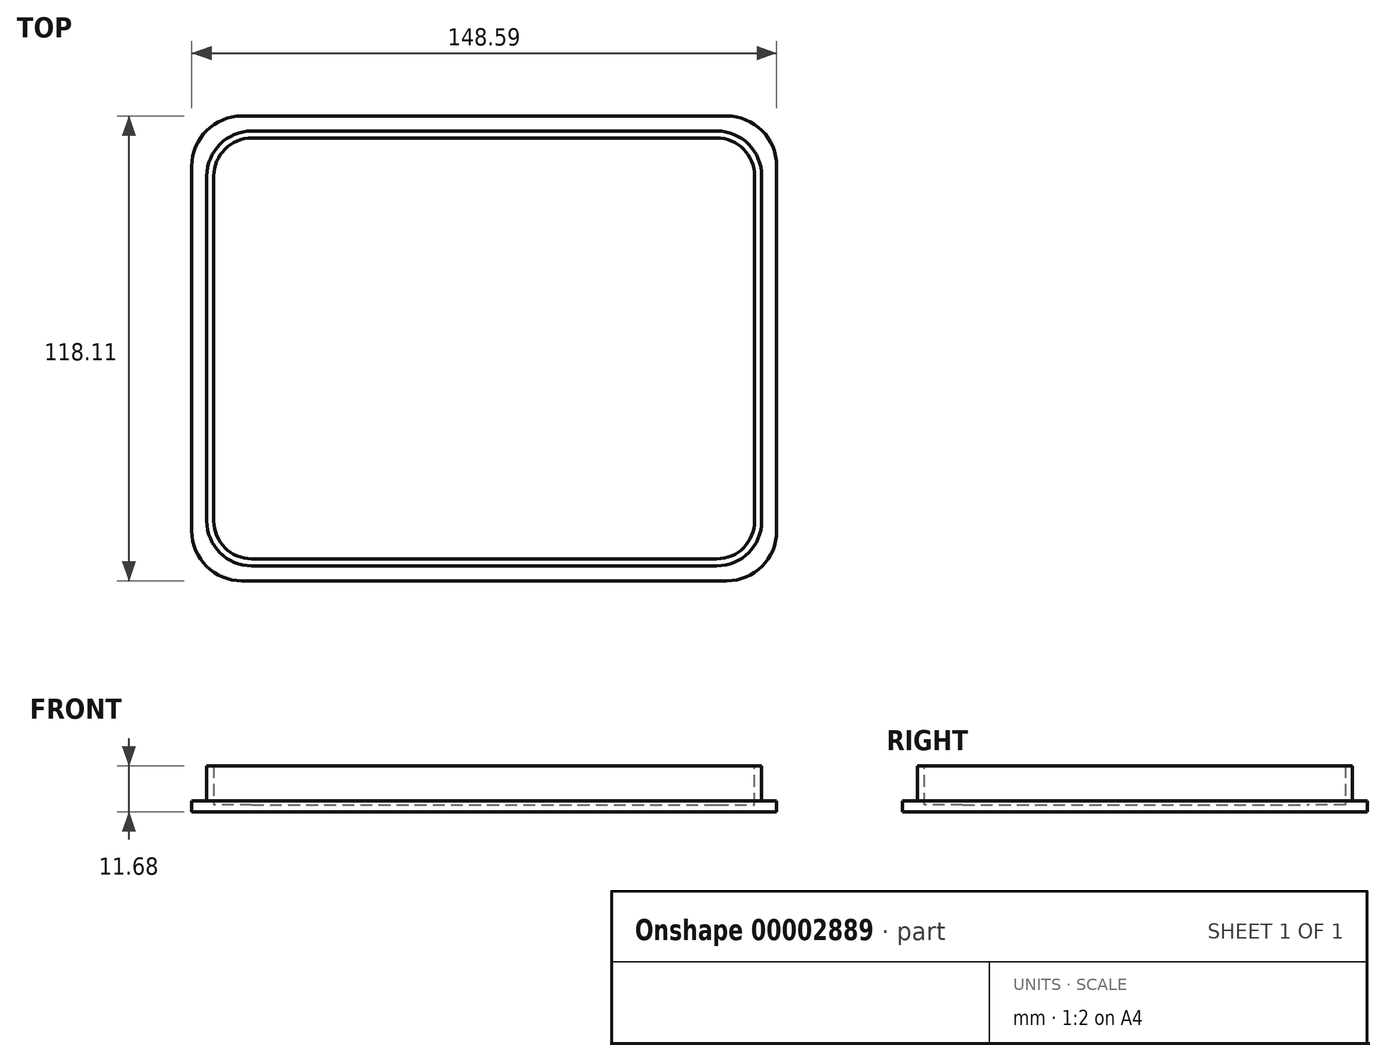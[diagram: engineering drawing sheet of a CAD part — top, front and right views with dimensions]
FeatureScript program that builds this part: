
annotation { "Feature Type Name" : "Feature", "Feature Type Description" : "" }
export const myFeature = defineFeature(function(context is Context, id is Id, definition is map)
    precondition{}
    {
        {
            var Q0;
            Q0=qCreatedBy(makeId("Top.planeOp"),FACE);
            var sketch = newSketch(context, id + "F0", { "sketchPlane" : qUnion([Q0])});
            skLineSegment(sketch, "E0.bottom", {"start": v(12.7, 0) * mm, "end": v(135.9, 0) * mm});
            skLineSegment(sketch, "E0.top", {"start": v(12.7, 118.11) * mm, "end": v(135.89, 118.11) * mm});
            skLineSegment(sketch, "E0.left", {"start": v(0, 12.7) * mm, "end": v(0, 105.41) * mm});
            skLineSegment(sketch, "E0.right", {"start": v(148.6, 12.7) * mm, "end": v(148.59, 105.41) * mm});
            skPoint(sketch, "E1.visualSharp", {"position": v(0, 118.11) * mm});
            skArc(sketch, "E1.filletArc", {"start": v(12.7, 118.11) * mm, "mid": v(3.72, 114.4) * mm, "end": v(0, 105.41) * mm});
            skPoint(sketch, "E2.visualSharp", {"position": v(148.59, 118.11) * mm});
            skArc(sketch, "E2.filletArc", {"start": v(148.59, 105.41) * mm, "mid": v(144.87, 114.4) * mm, "end": v(135.89, 118.11) * mm});
            skPoint(sketch, "E3.visualSharp", {"position": v(148.6, 0) * mm});
            skArc(sketch, "E3.filletArc", {"start": v(135.9, 0) * mm, "mid": v(144.87, 3.72) * mm, "end": v(148.6, 12.7) * mm});
            skPoint(sketch, "E4.visualSharp", {"position": v(0, 0) * mm});
            skArc(sketch, "E4.filletArc", {"start": v(0, 12.7) * mm, "mid": v(3.72, 3.72) * mm, "end": v(12.7, 0) * mm});
            skSolve(sketch);
        }
        {
            var Q0;
            Q0=makeQuery(id+"F0.imprint","IMPRINT",FACE,{"disambiguationData":[TD([[makeQuery(id+"F0.imprint","IMPRINT",EDGE,{"derivedFrom":sQuery(id+"F0.wireOp",EDGE,"E0.bottom")}),1.0]])]});
            extrude(context, id + "F1", {"entities" : qUnion([Q0]), "depth" : 2.8 * mm, "offsetDistance" : 25.4 * mm});
        }
        {
            var Q0;
            Q0=makeQuery(id+"F1.opExtrude","CAP_FACE",FACE,{"disambiguationData":[OSD([sQuery(id+"F0.wireOp",EDGE,"E0.bottom"),sQuery(id+"F0.wireOp",EDGE,"E0.top"),sQuery(id+"F0.wireOp",EDGE,"E0.left"),sQuery(id+"F0.wireOp",EDGE,"E0.right"),sQuery(id+"F0.wireOp",EDGE,"E1.filletArc"),sQuery(id+"F0.wireOp",EDGE,"E2.filletArc"),sQuery(id+"F0.wireOp",EDGE,"E3.filletArc"),sQuery(id+"F0.wireOp",EDGE,"E4.filletArc")])],"isStart":false});
            var sketch = newSketch(context, id + "F2", { "sketchPlane" : qUnion([Q0])});
            skLineSegment(sketch, "E5.0.0", {"start": v(135.89, 118.11) * mm, "end": v(12.7, 118.11) * mm});
            skArc(sketch, "E5.0.1", {"start": v(12.7, 118.11) * mm, "mid": v(3.72, 114.4) * mm, "end": v(0, 105.41) * mm});
            skLineSegment(sketch, "E5.0.2", {"start": v(0, 105.41) * mm, "end": v(0, 12.7) * mm});
            skArc(sketch, "E5.0.3", {"start": v(0, 12.7) * mm, "mid": v(3.72, 3.72) * mm, "end": v(12.7, 0) * mm});
            skLineSegment(sketch, "E5.0.4", {"start": v(12.7, 0) * mm, "end": v(135.9, 0) * mm});
            skArc(sketch, "E5.0.5", {"start": v(135.9, 0) * mm, "mid": v(144.87, 3.72) * mm, "end": v(148.6, 12.7) * mm});
            skLineSegment(sketch, "E5.0.6", {"start": v(148.6, 12.7) * mm, "end": v(148.6, 105.41) * mm});
            skArc(sketch, "E5.0.7", {"start": v(148.6, 105.41) * mm, "mid": v(144.87, 114.4) * mm, "end": v(135.89, 118.11) * mm});
            skLineSegment(sketch, "E6.0", {"start": v(133.35, 114.3) * mm, "end": v(15.24, 114.3) * mm});
            skLineSegment(sketch, "E6.1", {"start": v(144.78, 15.24) * mm, "end": v(144.78, 102.87) * mm});
            skLineSegment(sketch, "E6.2", {"start": v(15.24, 3.8) * mm, "end": v(133.35, 3.8) * mm});
            skLineSegment(sketch, "E6.3", {"start": v(3.8, 102.87) * mm, "end": v(3.8, 15.24) * mm});
            skPoint(sketch, "E7.visualSharp", {"position": v(3.8, 114.3) * mm});
            skArc(sketch, "E7.filletArc", {"start": v(15.24, 114.3) * mm, "mid": v(7.16, 110.95) * mm, "end": v(3.8, 102.87) * mm});
            skPoint(sketch, "E8.visualSharp", {"position": v(144.78, 114.3) * mm});
            skArc(sketch, "E8.filletArc", {"start": v(144.78, 102.87) * mm, "mid": v(141.43, 110.95) * mm, "end": v(133.35, 114.3) * mm});
            skPoint(sketch, "E9.visualSharp", {"position": v(144.78, 3.8) * mm});
            skArc(sketch, "E9.filletArc", {"start": v(133.35, 3.8) * mm, "mid": v(141.43, 7.16) * mm, "end": v(144.78, 15.24) * mm});
            skPoint(sketch, "E10.visualSharp", {"position": v(3.8, 3.8) * mm});
            skArc(sketch, "E10.filletArc", {"start": v(3.8, 15.24) * mm, "mid": v(7.16, 7.16) * mm, "end": v(15.24, 3.8) * mm});
            skSolve(sketch);
        }
        {
            var Q0;
            Q0=makeQuery(id+"F2.imprint","IMPRINT",FACE,{"disambiguationData":[TD([[makeQuery(id+"F2.imprint","IMPRINT",EDGE,{"derivedFrom":sQuery(id+"F2.wireOp",EDGE,"E6.0")}),1.0]])]});
            extrude(context, id + "F3", {"entities" : qUnion([Q0]), "operationType" : NewBodyOperationType.ADD, "depth" : 8.9 * mm, "offsetDistance" : 25.4 * mm});
        }
        {
            var Q0;
            Q0=makeQuery(id+"F3.opExtrude","CAP_FACE",FACE,{"disambiguationData":[OSD([sQuery(id+"F2.wireOp",EDGE,"E6.0"),sQuery(id+"F2.wireOp",EDGE,"E6.1"),sQuery(id+"F2.wireOp",EDGE,"E6.2"),sQuery(id+"F2.wireOp",EDGE,"E6.3"),sQuery(id+"F2.wireOp",EDGE,"E7.filletArc"),sQuery(id+"F2.wireOp",EDGE,"E8.filletArc"),sQuery(id+"F2.wireOp",EDGE,"E9.filletArc"),sQuery(id+"F2.wireOp",EDGE,"E10.filletArc")])],"isStart":false});
            shell(context, id + "F4", {"entities" : qUnion([Q0]), "thickness" : 1.78 * mm});
        }
    });
